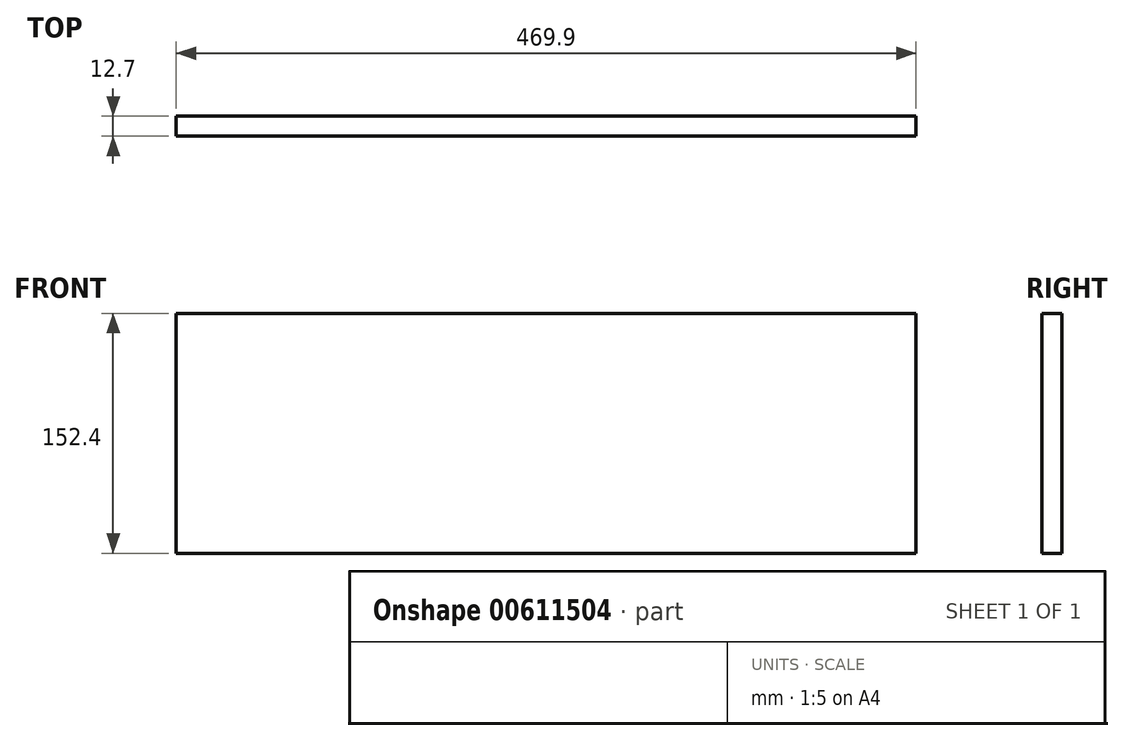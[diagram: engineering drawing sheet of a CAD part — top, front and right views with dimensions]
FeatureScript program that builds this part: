
annotation { "Feature Type Name" : "Feature", "Feature Type Description" : "" }
export const myFeature = defineFeature(function(context is Context, id is Id, definition is map)
    precondition{}
    {
        {
            var Q0;
            Q0=qCreatedBy(makeId("Front.planeOp"),FACE);
            var sketch = newSketch(context, id + "F0", { "sketchPlane" : qUnion([Q0])});
            skLineSegment(sketch, "E0.bottom", {"start": v(330.87, -49.63) * mm, "end": v(-139.03, -49.63) * mm});
            skLineSegment(sketch, "E0.top", {"start": v(330.87, 102.77) * mm, "end": v(-139.03, 102.77) * mm});
            skLineSegment(sketch, "E0.left", {"start": v(330.87, -49.63) * mm, "end": v(330.87, 102.77) * mm});
            skLineSegment(sketch, "E0.right", {"start": v(-139.03, -49.63) * mm, "end": v(-139.03, 102.77) * mm});
            skPoint(sketch, "E0.middle", {"position": v(95.92, 26.57) * mm});
            skSolve(sketch);
        }
        {
            var Q0;
            Q0=makeQuery(id+"F0.imprint","IMPRINT",FACE,{"disambiguationData":[TD([[makeQuery(id+"F0.imprint","IMPRINT",EDGE,{"derivedFrom":sQuery(id+"F0.wireOp",EDGE,"E0.bottom")}),-1.0]])]});
            extrude(context, id + "F1", {"entities" : qUnion([Q0]), "depth" : 12.7 * mm, "offsetDistance" : 25.4 * mm});
        }
    });
